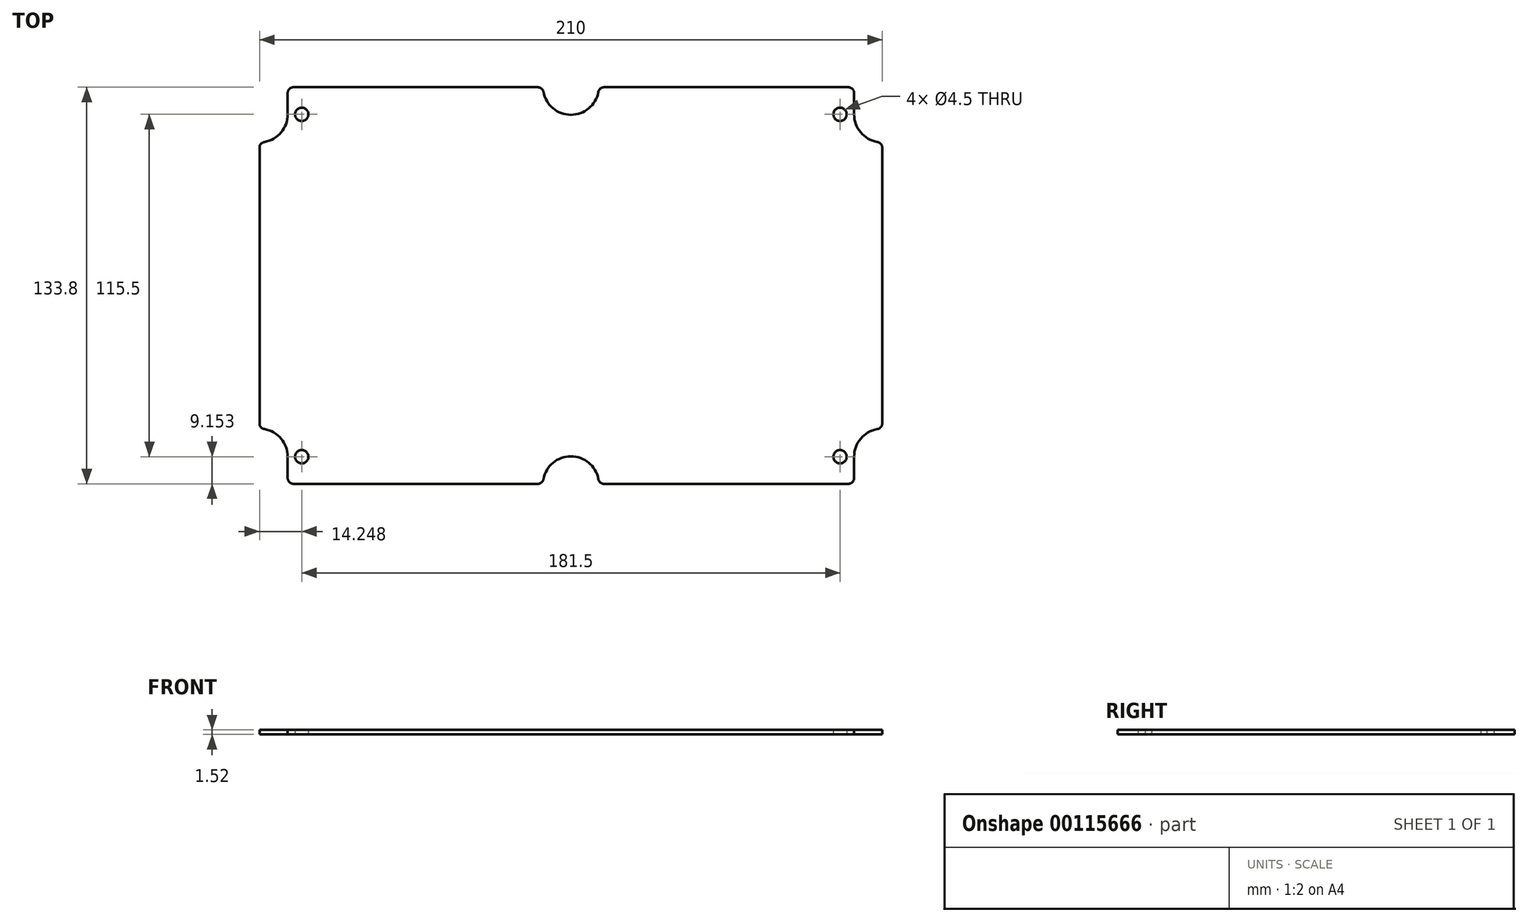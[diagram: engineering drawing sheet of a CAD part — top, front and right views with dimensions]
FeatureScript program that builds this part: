
annotation { "Feature Type Name" : "Feature", "Feature Type Description" : "" }
export const myFeature = defineFeature(function(context is Context, id is Id, definition is map)
    precondition{}
    {
        {
            var Q0;
            Q0=qCreatedBy(makeId("Top.planeOp"),FACE);
            var sketch = newSketch(context, id + "F0", { "sketchPlane" : qUnion([Q0])});
            skArc(sketch, "E0", {"start": v(-12.36, -65.68) * mm, "mid": v(-11.08, -65.22) * mm, "end": v(-10.4, -64.05) * mm});
            skArc(sketch, "E1", {"start": v(-96.65, -63.68) * mm, "mid": v(-96.07, -65.1) * mm, "end": v(-94.65, -65.68) * mm});
            skArc(sketch, "E2", {"start": v(-106.15, -45.24) * mm, "mid": v(-105.68, -46.53) * mm, "end": v(-104.49, -47.2) * mm});
            skArc(sketch, "E3", {"start": v(-104.49, 49.65) * mm, "mid": v(-105.68, 48.97) * mm, "end": v(-106.15, 47.68) * mm});
            skArc(sketch, "E4", {"start": v(-94.65, 68.12) * mm, "mid": v(-96.07, 67.54) * mm, "end": v(-96.65, 66.12) * mm});
            skArc(sketch, "E5", {"start": v(-10.4, 66.5) * mm, "mid": v(-11.08, 67.66) * mm, "end": v(-12.36, 68.12) * mm});
            skArc(sketch, "E6", {"start": v(10.05, 68.12) * mm, "mid": v(8.78, 67.66) * mm, "end": v(8.09, 66.5) * mm});
            skArc(sketch, "E7", {"start": v(94.35, 66.12) * mm, "mid": v(93.76, 67.54) * mm, "end": v(92.35, 68.12) * mm});
            skArc(sketch, "E8", {"start": v(103.85, 47.68) * mm, "mid": v(103.38, 48.97) * mm, "end": v(102.18, 49.65) * mm});
            skArc(sketch, "E9", {"start": v(102.18, -47.2) * mm, "mid": v(103.38, -46.53) * mm, "end": v(103.85, -45.24) * mm});
            skArc(sketch, "E10", {"start": v(8.09, -64.05) * mm, "mid": v(8.78, -65.22) * mm, "end": v(10.05, -65.68) * mm});
            skCircle(sketch, "E11", {"center": v(-91.9, 58.97) * mm, "radius": 2.25 * mm});
            skCircle(sketch, "E12", {"center": v(-91.9, -56.53) * mm, "radius": 2.25 * mm});
            skCircle(sketch, "E13", {"center": v(89.6, -56.53) * mm, "radius": 2.25 * mm});
            skCircle(sketch, "E14", {"center": v(89.6, 58.97) * mm, "radius": 2.25 * mm});
            skArc(sketch, "E15", {"start": v(92.35, -65.68) * mm, "mid": v(93.76, -65.1) * mm, "end": v(94.35, -63.68) * mm});
            skLineSegment(sketch, "E16", {"start": v(94.35, -63.68) * mm, "end": v(94.35, -56.48) * mm});
            skArc(sketch, "E17", {"start": v(102.18, -47.2) * mm, "mid": v(96.57, -50.4) * mm, "end": v(94.35, -56.48) * mm});
            skLineSegment(sketch, "E18", {"start": v(103.85, -45.24) * mm, "end": v(103.85, 47.68) * mm});
            skArc(sketch, "E19", {"start": v(94.35, 58.92) * mm, "mid": v(96.57, 52.86) * mm, "end": v(102.18, 49.65) * mm});
            skLineSegment(sketch, "E20", {"start": v(94.35, 58.92) * mm, "end": v(94.35, 66.12) * mm});
            skLineSegment(sketch, "E21", {"start": v(92.35, 68.12) * mm, "end": v(10.05, 68.12) * mm});
            skArc(sketch, "E22", {"start": v(-10.4, 66.5) * mm, "mid": v(-1.15, 58.82) * mm, "end": v(8.09, 66.5) * mm});
            skLineSegment(sketch, "E23", {"start": v(-12.36, 68.12) * mm, "end": v(-94.65, 68.12) * mm});
            skLineSegment(sketch, "E24", {"start": v(-96.65, 66.12) * mm, "end": v(-96.65, 58.92) * mm});
            skArc(sketch, "E25", {"start": v(-104.49, 49.65) * mm, "mid": v(-98.87, 52.86) * mm, "end": v(-96.65, 58.92) * mm});
            skLineSegment(sketch, "E26", {"start": v(-106.15, 47.68) * mm, "end": v(-106.15, -45.24) * mm});
            skArc(sketch, "E27", {"start": v(-96.65, -56.48) * mm, "mid": v(-98.87, -50.4) * mm, "end": v(-104.49, -47.2) * mm});
            skLineSegment(sketch, "E28", {"start": v(-96.65, -56.48) * mm, "end": v(-96.65, -63.68) * mm});
            skLineSegment(sketch, "E29", {"start": v(-94.65, -65.68) * mm, "end": v(-12.36, -65.68) * mm});
            skArc(sketch, "E30", {"start": v(8.09, -64.05) * mm, "mid": v(-1.15, -56.38) * mm, "end": v(-10.4, -64.05) * mm});
            skLineSegment(sketch, "E31", {"start": v(10.05, -65.68) * mm, "end": v(92.35, -65.68) * mm});
            skSolve(sketch);
        }
        {
            var Q0;
            Q0=makeQuery(id+"F0.imprint","IMPRINT",FACE,{"disambiguationData":[TD([[makeQuery(id+"F0.imprint","IMPRINT",EDGE,{"derivedFrom":sQuery(id+"F0.wireOp",EDGE,"E0")}),1.0]])]});
            extrude(context, id + "F1", {"entities" : qUnion([Q0]), "depth" : 1.52 * mm});
        }
    });
